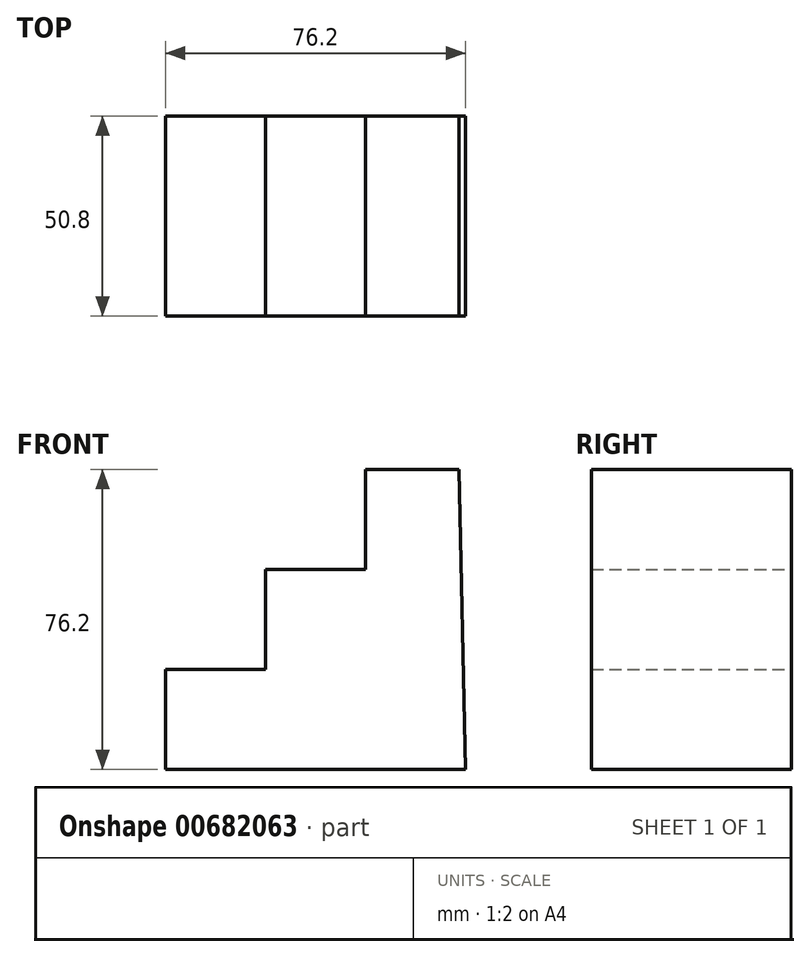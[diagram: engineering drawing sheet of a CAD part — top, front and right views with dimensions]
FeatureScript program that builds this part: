
annotation { "Feature Type Name" : "Feature", "Feature Type Description" : "" }
export const myFeature = defineFeature(function(context is Context, id is Id, definition is map)
    precondition{}
    {
        {
            var Q0;
            Q0=qCreatedBy(makeId("Front.planeOp"),FACE);
            var sketch = newSketch(context, id + "F0", { "sketchPlane" : qUnion([Q0])});
            skLineSegment(sketch, "E0", {"start": v(25.4, 44.78) * mm, "end": v(27.03, -31.4) * mm});
            skLineSegment(sketch, "E1", {"start": v(27.03, -31.4) * mm, "end": v(-49.17, -31.4) * mm});
            skLineSegment(sketch, "E2", {"start": v(-49.17, -31.4) * mm, "end": v(-49.17, -6) * mm});
            skLineSegment(sketch, "E3", {"start": v(-49.17, -6) * mm, "end": v(-23.77, -6) * mm});
            skLineSegment(sketch, "E4", {"start": v(-23.77, -6) * mm, "end": v(-23.77, 19.4) * mm});
            skLineSegment(sketch, "E5", {"start": v(-23.77, 19.4) * mm, "end": v(1.63, 19.4) * mm});
            skLineSegment(sketch, "E6", {"start": v(1.63, 19.4) * mm, "end": v(1.63, 44.8) * mm});
            skLineSegment(sketch, "E7", {"start": v(1.63, 44.8) * mm, "end": v(25.4, 44.78) * mm});
            skSolve(sketch);
        }
        {
            var Q0;
            Q0 = qSketchRegion(id + "F0", true);
            extrude(context, id + "F1", {"entities" : qUnion([Q0]), "depth" : 50.8 * mm, "offsetDistance" : 25.4 * mm});
        }
    });
